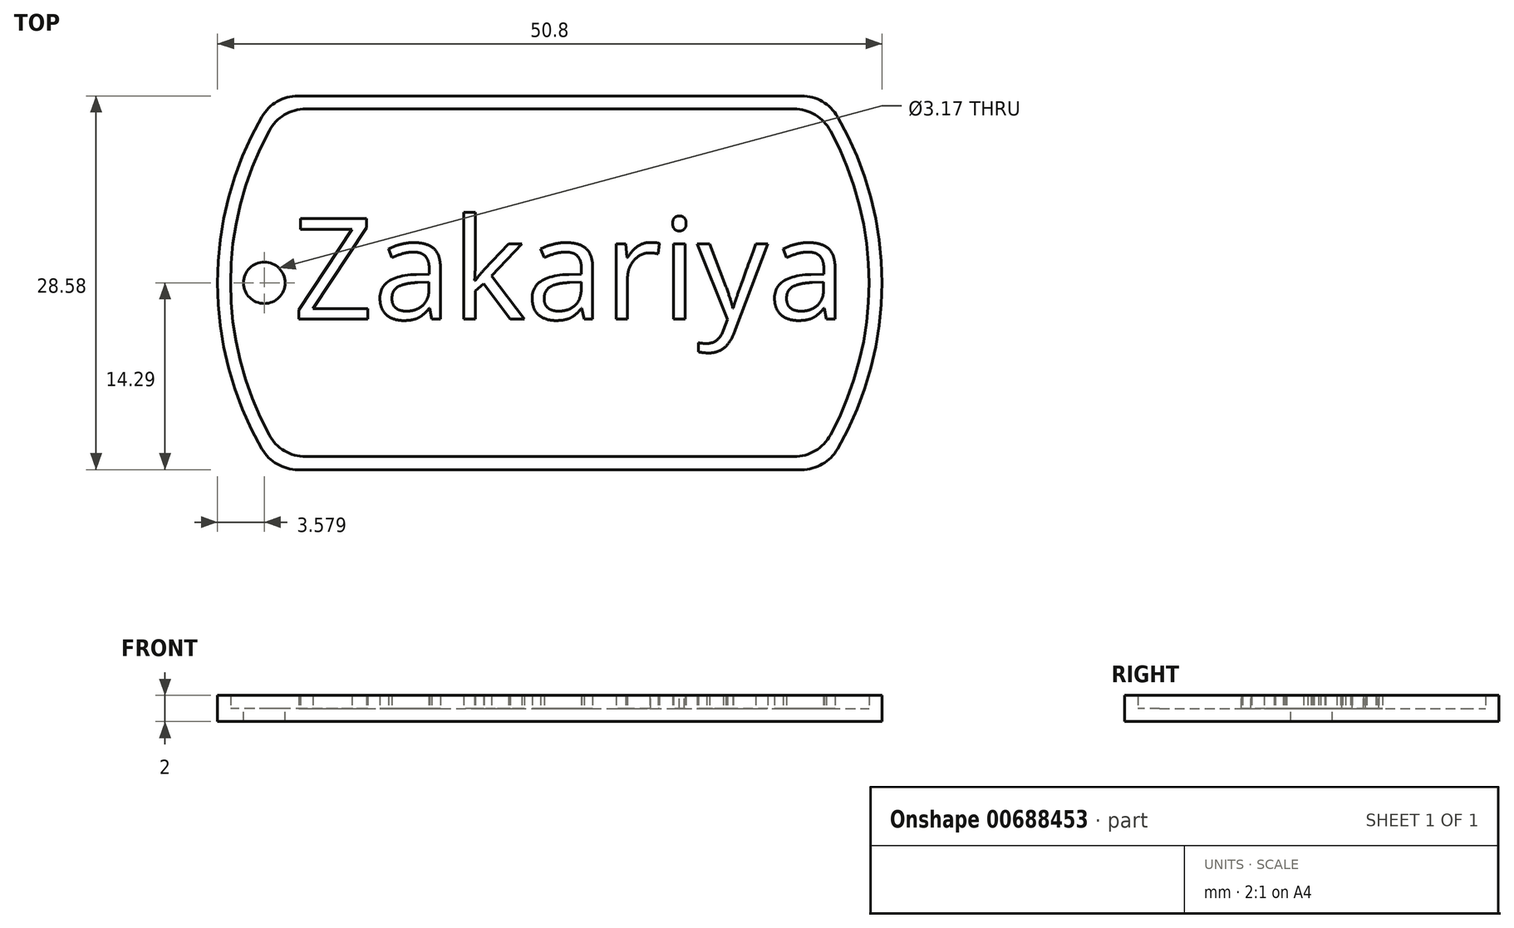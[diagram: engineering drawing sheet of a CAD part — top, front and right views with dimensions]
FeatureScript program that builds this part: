
annotation { "Feature Type Name" : "Feature", "Feature Type Description" : "" }
export const myFeature = defineFeature(function(context is Context, id is Id, definition is map)
    precondition{}
    {
        {
            var Q0;
            Q0=qCreatedBy(makeId("Top.planeOp"),FACE);
            var sketch = newSketch(context, id + "F0", { "sketchPlane" : qUnion([Q0])});
            skArc(sketch, "E0", {"start": v(-22, 12.7) * mm, "mid": v(-25.4, 0) * mm, "end": v(-22, -12.7) * mm});
            skLineSegment(sketch, "E1.top", {"start": v(-19.25, -14.29) * mm, "end": v(19.25, -14.29) * mm});
            skArc(sketch, "E2.trimOffspring", {"start": v(22, -12.7) * mm, "mid": v(25.4, 0) * mm, "end": v(22, 12.7) * mm});
            skLineSegment(sketch, "E3", {"start": v(-19.25, 14.29) * mm, "end": v(19.25, 14.29) * mm});
            skPoint(sketch, "E4.visualSharp", {"position": v(-21, 14.29) * mm});
            skArc(sketch, "E4.filletArc", {"start": v(-19.25, 14.29) * mm, "mid": v(-20.83, 13.86) * mm, "end": v(-22, 12.7) * mm});
            skPoint(sketch, "E5.visualSharp", {"position": v(21, 14.29) * mm});
            skArc(sketch, "E5.filletArc", {"start": v(22, 12.7) * mm, "mid": v(20.83, 13.86) * mm, "end": v(19.25, 14.29) * mm});
            skPoint(sketch, "E6.visualSharp", {"position": v(21, -14.29) * mm});
            skArc(sketch, "E6.filletArc", {"start": v(19.25, -14.29) * mm, "mid": v(20.83, -13.86) * mm, "end": v(22, -12.7) * mm});
            skPoint(sketch, "E7.visualSharp", {"position": v(-21, -14.29) * mm});
            skArc(sketch, "E7.filletArc", {"start": v(-22, -12.7) * mm, "mid": v(-20.83, -13.86) * mm, "end": v(-19.25, -14.29) * mm});
            skSolve(sketch);
        }
        {
            var Q0;
            Q0=makeQuery(id+"F0.imprint","IMPRINT",FACE,{"disambiguationData":[TD([[makeQuery(id+"F0.imprint","IMPRINT",EDGE,{"derivedFrom":sQuery(id+"F0.wireOp",EDGE,"E0")}),1.0]])]});
            extrude(context, id + "F1", {"entities" : qUnion([Q0]), "depth" : 1 * mm, "offsetDistance" : 25.4 * mm});
        }
        {
            var Q0;
            Q0=makeQuery(id+"F1.opExtrude","CAP_FACE",FACE,{"disambiguationData":[OSD([sQuery(id+"F0.wireOp",EDGE,"E0"),sQuery(id+"F0.wireOp",EDGE,"E1.top"),sQuery(id+"F0.wireOp",EDGE,"E2.trimOffspring"),sQuery(id+"F0.wireOp",EDGE,"E3"),sQuery(id+"F0.wireOp",EDGE,"E4.filletArc"),sQuery(id+"F0.wireOp",EDGE,"E5.filletArc"),sQuery(id+"F0.wireOp",EDGE,"E6.filletArc"),sQuery(id+"F0.wireOp",EDGE,"E7.filletArc")])],"isStart":false});
            var sketch = newSketch(context, id + "F2", { "sketchPlane" : qUnion([Q0])});
            skLineSegment(sketch, "E8.0", {"start": v(-18.66, 13.29) * mm, "end": v(18.66, 13.29) * mm});
            skArc(sketch, "E8.1", {"start": v(-21.45, 11.63) * mm, "mid": v(-24.4, 0) * mm, "end": v(-21.45, -11.63) * mm});
            skLineSegment(sketch, "E8.2", {"start": v(-18.66, -13.29) * mm, "end": v(18.66, -13.29) * mm});
            skArc(sketch, "E8.3", {"start": v(21.45, -11.63) * mm, "mid": v(24.4, 0) * mm, "end": v(21.45, 11.63) * mm});
            skPoint(sketch, "E9.visualSharp", {"position": v(-20.46, 13.29) * mm});
            skArc(sketch, "E9.filletArc", {"start": v(-18.66, 13.29) * mm, "mid": v(-20.29, 12.84) * mm, "end": v(-21.45, 11.63) * mm});
            skPoint(sketch, "E10.visualSharp", {"position": v(20.46, 13.29) * mm});
            skArc(sketch, "E10.filletArc", {"start": v(21.45, 11.63) * mm, "mid": v(20.29, 12.84) * mm, "end": v(18.66, 13.29) * mm});
            skPoint(sketch, "E11.visualSharp", {"position": v(20.46, -13.29) * mm});
            skArc(sketch, "E11.filletArc", {"start": v(18.66, -13.29) * mm, "mid": v(20.29, -12.84) * mm, "end": v(21.45, -11.63) * mm});
            skPoint(sketch, "E12.visualSharp", {"position": v(-20.46, -13.29) * mm});
            skArc(sketch, "E12.filletArc", {"start": v(-21.45, -11.63) * mm, "mid": v(-20.29, -12.84) * mm, "end": v(-18.66, -13.29) * mm});
            skLineSegment(sketch, "E13.0", {"start": v(-19.25, 14.29) * mm, "end": v(19.25, 14.29) * mm});
            skArc(sketch, "E13.1", {"start": v(-22, 12.7) * mm, "mid": v(-25.4, 0) * mm, "end": v(-22, -12.7) * mm});
            skLineSegment(sketch, "E13.2", {"start": v(-19.25, -14.29) * mm, "end": v(19.25, -14.29) * mm});
            skArc(sketch, "E13.3", {"start": v(22, -12.7) * mm, "mid": v(25.4, 0) * mm, "end": v(22, 12.7) * mm});
            skPoint(sketch, "E14.visualSharp", {"position": v(-21, -14.29) * mm});
            skArc(sketch, "E14.filletArc", {"start": v(-22, -12.7) * mm, "mid": v(-20.83, -13.86) * mm, "end": v(-19.25, -14.29) * mm});
            skPoint(sketch, "E15.visualSharp", {"position": v(21, -14.29) * mm});
            skArc(sketch, "E15.filletArc", {"start": v(19.25, -14.29) * mm, "mid": v(20.83, -13.86) * mm, "end": v(22, -12.7) * mm});
            skPoint(sketch, "E16.visualSharp", {"position": v(21, 14.29) * mm});
            skArc(sketch, "E16.filletArc", {"start": v(22, 12.7) * mm, "mid": v(20.83, 13.86) * mm, "end": v(19.25, 14.29) * mm});
            skPoint(sketch, "E17.visualSharp", {"position": v(-21, 14.29) * mm});
            skArc(sketch, "E17.filletArc", {"start": v(-19.25, 14.29) * mm, "mid": v(-20.83, 13.86) * mm, "end": v(-22, 12.7) * mm});
            skSolve(sketch);
        }
        {
            var Q0;
            Q0=makeQuery(id+"F2.imprint","IMPRINT",FACE,{"disambiguationData":[TD([[makeQuery(id+"F2.imprint","IMPRINT",EDGE,{"derivedFrom":sQuery(id+"F2.wireOp",EDGE,"E8.0")}),1.0]])]});
            extrude(context, id + "F3", {"entities" : qUnion([Q0]), "operationType" : NewBodyOperationType.ADD, "depth" : 1 * mm, "offsetDistance" : 25.4 * mm});
        }
        {
            var Q0;
            Q0=makeQuery(id+"F1.opExtrude","CAP_FACE",FACE,{"disambiguationData":[OSD([sQuery(id+"F0.wireOp",EDGE,"E0"),sQuery(id+"F0.wireOp",EDGE,"E1.top"),sQuery(id+"F0.wireOp",EDGE,"E2.trimOffspring"),sQuery(id+"F0.wireOp",EDGE,"E3"),sQuery(id+"F0.wireOp",EDGE,"E4.filletArc"),sQuery(id+"F0.wireOp",EDGE,"E5.filletArc"),sQuery(id+"F0.wireOp",EDGE,"E6.filletArc"),sQuery(id+"F0.wireOp",EDGE,"E7.filletArc")])],"isStart":false});
            var sketch = newSketch(context, id + "F4", { "sketchPlane" : qUnion([Q0])});
            skCircle(sketch, "E18", {"center": v(-21.82, 0) * mm, "radius": 1.59 * mm});
            skSolve(sketch);
        }
        {
            var Q0;
            Q0=makeQuery(id+"F4.imprint","IMPRINT",FACE,{"disambiguationData":[TD([[makeQuery(id+"F4.imprint","IMPRINT",EDGE,{"derivedFrom":sQuery(id+"F4.wireOp",EDGE,"E18")}),1.0]])]});
            extrude(context, id + "F5", {"entities" : qUnion([Q0]), "operationType" : NewBodyOperationType.REMOVE, "oppositeDirection" : true, "depth" : 1 * mm, "offsetDistance" : 25.4 * mm});
        }
        {
            var Q0;
            Q0=makeQuery(id+"F2.imprint","IMPRINT",FACE,{"disambiguationData":[TD([[makeQuery(id+"F2.imprint","IMPRINT",EDGE,{"derivedFrom":sQuery(id+"F2.wireOp",EDGE,"E8.0")}),-1.0]])]});
            var sketch = newSketch(context, id + "F6", { "sketchPlane" : qUnion([Q0])});
            skText(sketch, "E19", { "text": "Zakariya", "fontName": "OpenSans-Regular.ttf"});
            const initialGuessF6  = {"E19": [-0.01962, -0.00278, 1, 0, 0.00775]};
            skSetInitialGuess(sketch, initialGuessF6);
            skSolve(sketch);
        }
        {
            var Q0;
            Q0 = qSketchRegion(id + "F6", true);
            extrude(context, id + "F7", {"entities" : qUnion([Q0]), "operationType" : NewBodyOperationType.ADD, "depth" : 1 * mm, "offsetDistance" : 25.4 * mm});
        }
    });
